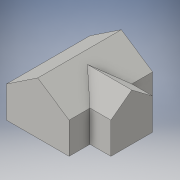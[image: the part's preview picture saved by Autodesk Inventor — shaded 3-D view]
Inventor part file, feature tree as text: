
AUTODESK INVENTOR PART (.ipt)
format: ipt  version: 2016 (Build 200138000, 138)  size: 108,544 bytes
history: native  units: in
note: dims shown in document units (in); Inventor stores cm internally (conversion verified against a paired STEP export)
features: extrude x2, sketch x2
ambient origin geometry x8: Origin, YZ Plane, XZ Plane, XY Plane, X Axis, Y Axis, Z Axis, Center Point
bodies: Solid1 (feature_tree)
feature tree (4):
  extrude  "Extrusion1"  Depth=0.75in
  extrude  "Extrusion2"  Depth=0.5in
  sketch  "Sketch1"  dims[d0=0.75in d1=0.75in]
  sketch  "Sketch2"  dims[d2=1.5in d3=0.5in d4=0.75in d5=2.0in d6=0.0in d7=0.5in d8=0.5in d9=0.375in d10=0.5in d11=0.5in d12=0.7in d13=0.0in d14=0.0in]
